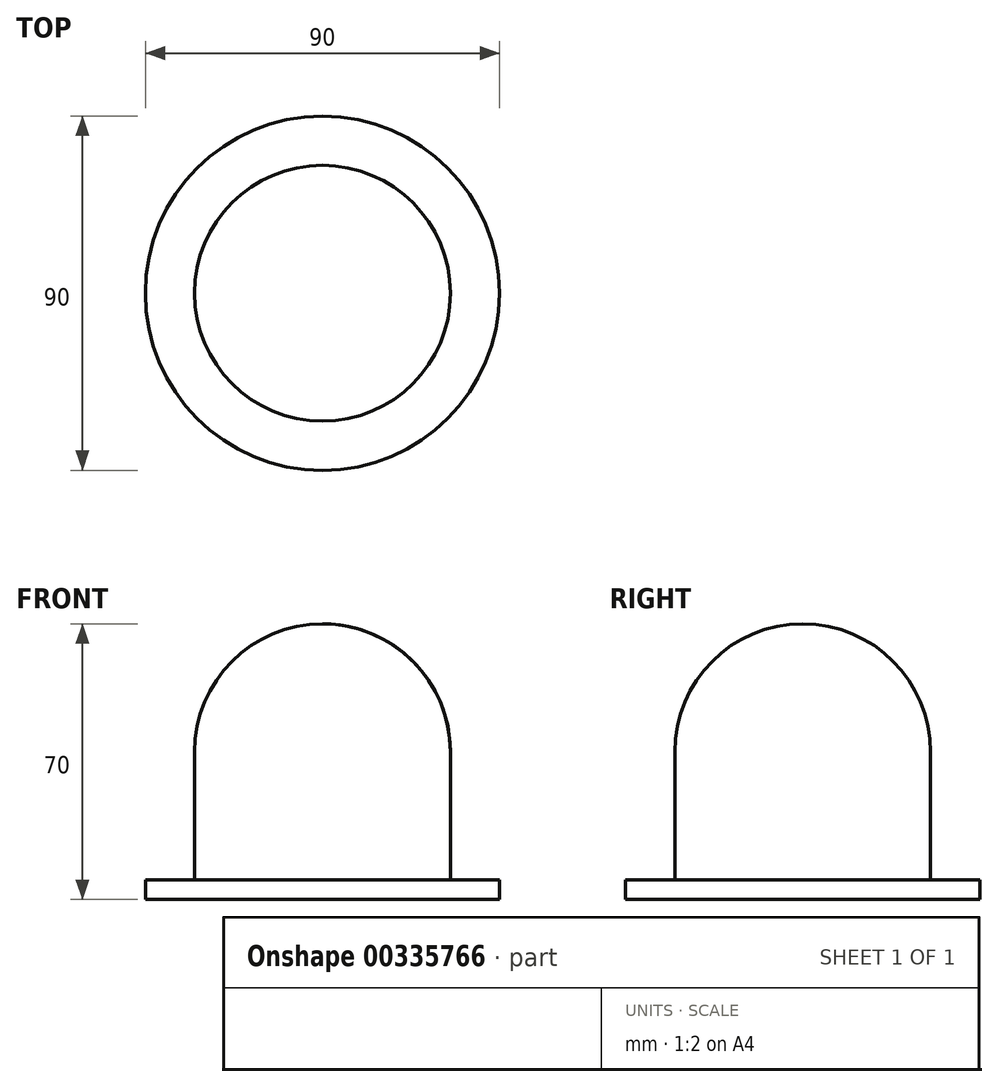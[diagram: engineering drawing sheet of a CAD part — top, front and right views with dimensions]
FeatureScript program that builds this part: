
annotation { "Feature Type Name" : "Feature", "Feature Type Description" : "" }
export const myFeature = defineFeature(function(context is Context, id is Id, definition is map)
    precondition{}
    {
        {
            var Q0;
            Q0=qCreatedBy(makeId("Front.planeOp"),FACE);
            var sketch = newSketch(context, id + "F0", { "sketchPlane" : qUnion([Q0])});
            skLineSegment(sketch, "E0", {"start": v(0, 0) * mm, "end": v(45, 0) * mm});
            skLineSegment(sketch, "E1", {"start": v(45, 0) * mm, "end": v(45, 5) * mm});
            skLineSegment(sketch, "E2", {"start": v(45, 5) * mm, "end": v(0, 5) * mm});
            skLineSegment(sketch, "E3", {"start": v(0, 5) * mm, "end": v(0, 0) * mm});
            skLineSegment(sketch, "E4", {"start": v(0, 0) * mm, "end": v(0, -30.24) * mm, "construction": true});
            skLineSegment(sketch, "E5", {"start": v(32.5, 5) * mm, "end": v(32.5, 37.5) * mm});
            skArc(sketch, "E6", {"start": v(32.5, 37.5) * mm, "mid": v(22.98, 60.48) * mm, "end": v(0, 70) * mm});
            skLineSegment(sketch, "E7", {"start": v(0, 70) * mm, "end": v(0, 5) * mm});
            skLineSegment(sketch, "E8", {"start": v(0, 70) * mm, "end": v(32.5, 70) * mm, "construction": true});
            skSolve(sketch);
        }
        {
            var Q0;
            Q0=makeQuery(id+"F0.imprint","IMPRINT",FACE,{"disambiguationData":[TD([[makeQuery(id+"F0.imprint","IMPRINT",EDGE,{"derivedFrom":sQuery(id+"F0.wireOp",EDGE,"E0")}),1.0]])]});
            var Q1;
            Q1=sQuery(id+"F0.wireOp",EDGE,"E4");
            revolve(context, id + "F1", {"entities" : qUnion([Q0]), "axis" : qUnion([Q1]), "revolveType" : RevolveType.FULL});
        }
        {
            var Q0;
            {var subQ2=sQuery(id+"F0.wireOp",EDGE,"E5");Q0=makeQuery(id+"F0.imprint","IMPRINT",FACE,{"disambiguationData":[TD([[makeQuery(id+"F0.imprint","IMPRINT",EDGE,{"derivedFrom":subQ2}),1.0]])]});}
            var Q1;
            Q1=sQuery(id+"F0.wireOp",EDGE,"E4");
            revolve(context, id + "F2", {"entities" : qUnion([Q0]), "axis" : qUnion([Q1]), "revolveType" : RevolveType.FULL});
        }
    });
